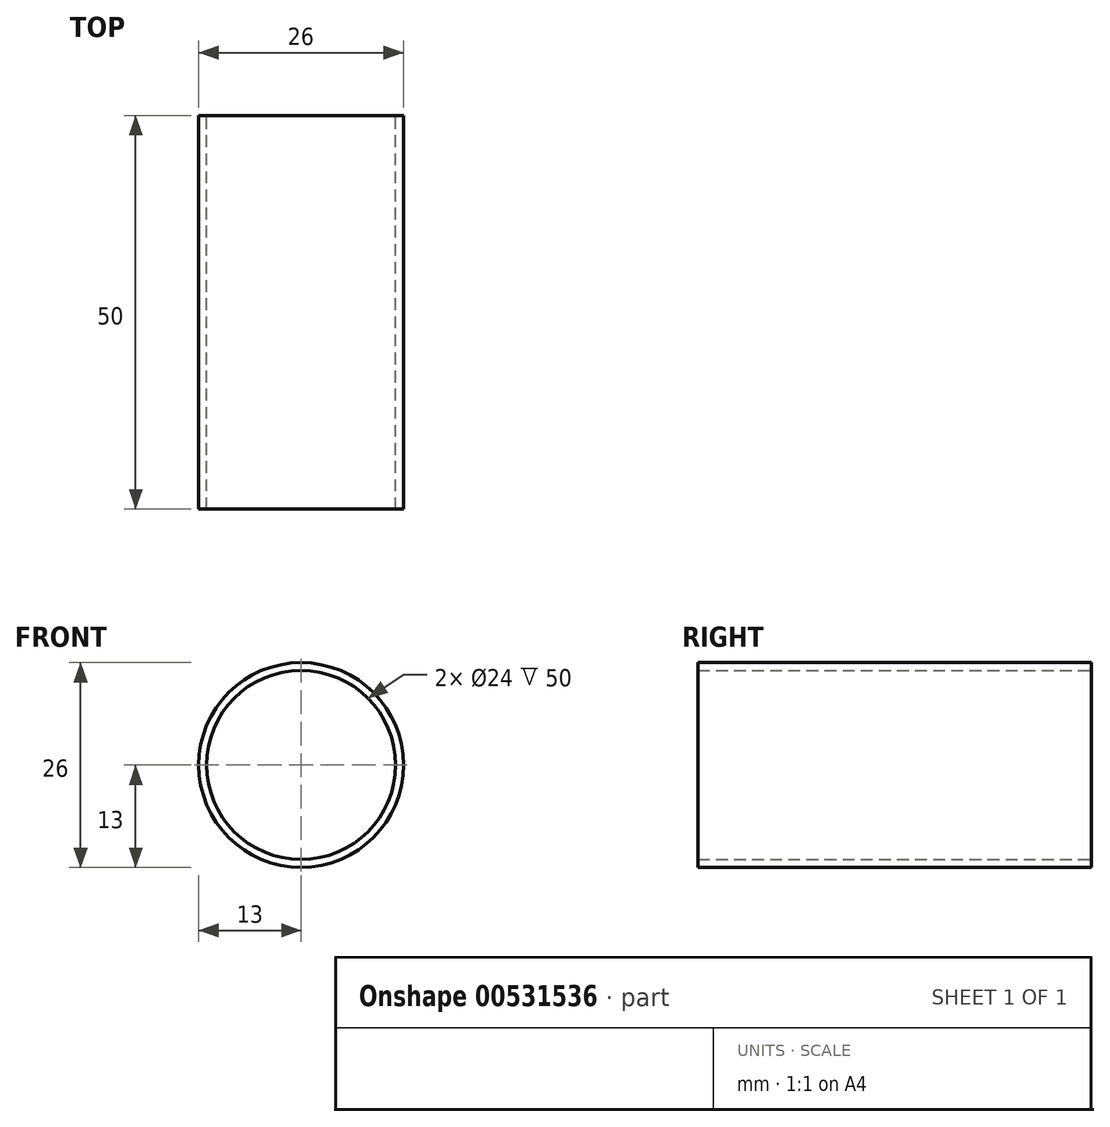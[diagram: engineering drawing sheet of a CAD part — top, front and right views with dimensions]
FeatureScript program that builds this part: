
annotation { "Feature Type Name" : "Feature", "Feature Type Description" : "" }
export const myFeature = defineFeature(function(context is Context, id is Id, definition is map)
    precondition{}
    {
        {
            var Q0;
            Q0=qCreatedBy(makeId("Front.planeOp"),FACE);
            var sketch = newSketch(context, id + "F0", { "sketchPlane" : qUnion([Q0])});
            skCircle(sketch, "E0", {"center": v(0, 0) * mm, "radius": 13 * mm});
            skCircle(sketch, "E1", {"center": v(0, 0) * mm, "radius": 12 * mm});
            skSolve(sketch);
        }
        {
            var Q0;
            Q0=makeQuery(id+"F0.imprint","IMPRINT",FACE,{"disambiguationData":[TD([[makeQuery(id+"F0.imprint","IMPRINT",EDGE,{"derivedFrom":sQuery(id+"F0.wireOp",EDGE,"E0")}),1.0]])]});
            extrude(context, id + "F1", {"entities" : qUnion([Q0]), "depth" : 50 * mm, "offsetDistance" : 25 * mm});
        }
    });
